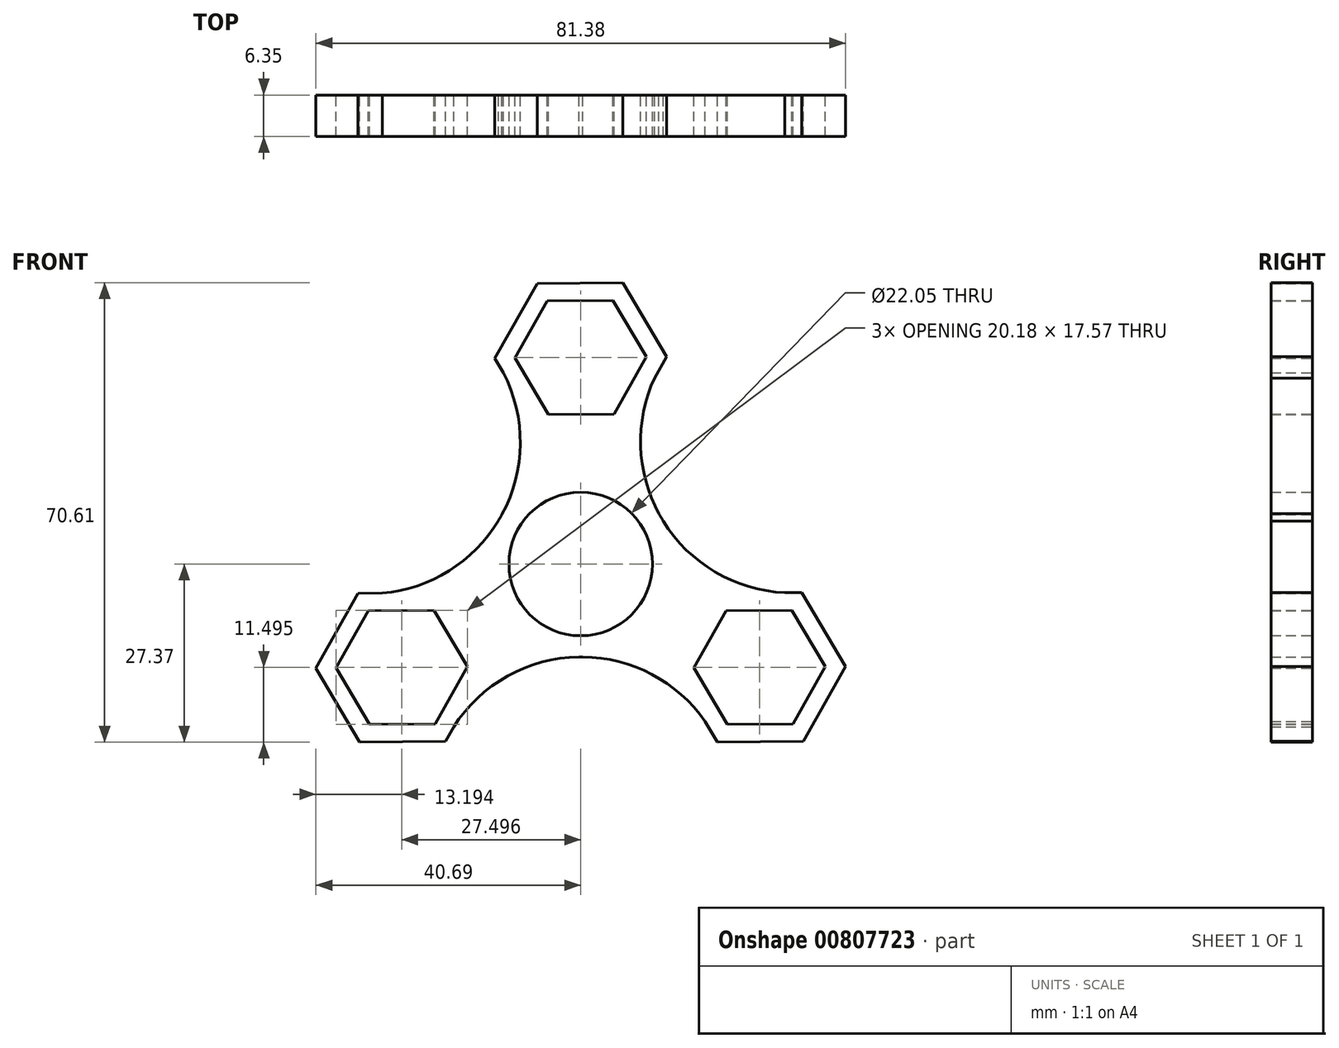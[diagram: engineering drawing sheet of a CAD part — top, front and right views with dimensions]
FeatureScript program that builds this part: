
annotation { "Feature Type Name" : "Feature", "Feature Type Description" : "" }
export const myFeature = defineFeature(function(context is Context, id is Id, definition is map)
    precondition{}
    {
        {
            var Q0;
            Q0=qCreatedBy(makeId("Front.planeOp"),FACE);
            var sketch = newSketch(context, id + "F0", { "sketchPlane" : qUnion([Q0])});
            skCircle(sketch, "E0", {"center": v(0, 0) * mm, "radius": 11.02 * mm});
            skCircle(sketch, "E1", {"center": v(0, 0) * mm, "radius": 14.29 * mm});
            skCircle(sketch, "E2.cCircle", {"center": v(0, 31.75) * mm, "radius": 11.43 * mm, "construction": true});
            skLineSegment(sketch, "E2.0", {"start": v(13.2, 31.87) * mm, "end": v(6.7, 20.38) * mm});
            skLineSegment(sketch, "E2.1", {"start": v(6.7, 20.38) * mm, "end": v(-6.5, 20.26) * mm});
            skLineSegment(sketch, "E2.2", {"start": v(-6.5, 20.26) * mm, "end": v(-13.2, 31.63) * mm});
            skLineSegment(sketch, "E2.3", {"start": v(-13.2, 31.63) * mm, "end": v(-6.7, 43.12) * mm});
            skLineSegment(sketch, "E2.4", {"start": v(-6.7, 43.12) * mm, "end": v(6.5, 43.24) * mm});
            skLineSegment(sketch, "E2.5", {"start": v(6.5, 43.24) * mm, "end": v(13.2, 31.87) * mm});
            skPoint(sketch, "E2.0.midPoint", {"position": v(9.95, 26.13) * mm});
            skCircle(sketch, "E3.cCircle", {"center": v(0, 31.75) * mm, "radius": 8.74 * mm, "construction": true});
            skLineSegment(sketch, "E3.0", {"start": v(-10.09, 31.66) * mm, "end": v(-5.13, 40.44) * mm});
            skLineSegment(sketch, "E3.1", {"start": v(-5.13, 40.44) * mm, "end": v(4.96, 40.53) * mm});
            skLineSegment(sketch, "E3.2", {"start": v(4.96, 40.53) * mm, "end": v(10.09, 31.84) * mm});
            skLineSegment(sketch, "E3.3", {"start": v(10.09, 31.84) * mm, "end": v(5.13, 23.06) * mm});
            skLineSegment(sketch, "E3.4", {"start": v(5.13, 23.06) * mm, "end": v(-4.96, 22.97) * mm});
            skLineSegment(sketch, "E3.5", {"start": v(-4.96, 22.97) * mm, "end": v(-10.09, 31.66) * mm});
            skPoint(sketch, "E3.0.midPoint", {"position": v(-7.6, 36.05) * mm});
            skCircle(sketch, "E4.1.0", {"center": v(-27.5, -15.87) * mm, "radius": 8.74 * mm, "construction": true});
            skLineSegment(sketch, "E4.1.1", {"start": v(-22.53, -7.1) * mm, "end": v(-17.4, -15.78) * mm});
            skLineSegment(sketch, "E4.1.2", {"start": v(-17.4, -15.78) * mm, "end": v(-22.37, -24.56) * mm});
            skLineSegment(sketch, "E4.1.3", {"start": v(-22.37, -24.56) * mm, "end": v(-32.46, -24.66) * mm});
            skLineSegment(sketch, "E4.1.4", {"start": v(-32.46, -24.66) * mm, "end": v(-37.59, -15.97) * mm});
            skLineSegment(sketch, "E4.1.5", {"start": v(-37.59, -15.97) * mm, "end": v(-32.62, -7.19) * mm});
            skLineSegment(sketch, "E4.1.6", {"start": v(-32.62, -7.19) * mm, "end": v(-22.53, -7.1) * mm});
            skLineSegment(sketch, "E4.1.7", {"start": v(-34.2, -4.5) * mm, "end": v(-21, -4.38) * mm});
            skCircle(sketch, "E4.1.8", {"center": v(-27.5, -15.87) * mm, "radius": 11.43 * mm, "construction": true});
            skLineSegment(sketch, "E4.1.9", {"start": v(-40.7, -16) * mm, "end": v(-34.2, -4.5) * mm});
            skLineSegment(sketch, "E4.1.10", {"start": v(-33.99, -27.37) * mm, "end": v(-40.7, -16) * mm});
            skLineSegment(sketch, "E4.1.11", {"start": v(-20.8, -27.24) * mm, "end": v(-33.99, -27.37) * mm});
            skLineSegment(sketch, "E4.1.12", {"start": v(-14.3, -15.75) * mm, "end": v(-20.8, -27.24) * mm});
            skLineSegment(sketch, "E4.1.13", {"start": v(-21, -4.38) * mm, "end": v(-14.3, -15.75) * mm});
            skCircle(sketch, "E4.2.0", {"center": v(27.5, -15.88) * mm, "radius": 8.74 * mm, "construction": true});
            skLineSegment(sketch, "E4.2.1", {"start": v(17.4, -15.97) * mm, "end": v(22.37, -7.19) * mm});
            skLineSegment(sketch, "E4.2.2", {"start": v(22.37, -7.19) * mm, "end": v(32.46, -7.1) * mm});
            skLineSegment(sketch, "E4.2.3", {"start": v(32.46, -7.1) * mm, "end": v(37.59, -15.78) * mm});
            skLineSegment(sketch, "E4.2.4", {"start": v(37.59, -15.78) * mm, "end": v(32.62, -24.56) * mm});
            skLineSegment(sketch, "E4.2.5", {"start": v(32.62, -24.56) * mm, "end": v(22.53, -24.66) * mm});
            skLineSegment(sketch, "E4.2.6", {"start": v(22.53, -24.66) * mm, "end": v(17.4, -15.97) * mm});
            skLineSegment(sketch, "E4.2.7", {"start": v(21, -27.37) * mm, "end": v(14.3, -16) * mm});
            skCircle(sketch, "E4.2.8", {"center": v(27.5, -15.88) * mm, "radius": 11.43 * mm, "construction": true});
            skLineSegment(sketch, "E4.2.9", {"start": v(34.2, -27.24) * mm, "end": v(21, -27.37) * mm});
            skLineSegment(sketch, "E4.2.10", {"start": v(40.7, -15.75) * mm, "end": v(34.2, -27.24) * mm});
            skLineSegment(sketch, "E4.2.11", {"start": v(33.99, -4.38) * mm, "end": v(40.7, -15.75) * mm});
            skLineSegment(sketch, "E4.2.12", {"start": v(20.8, -4.5) * mm, "end": v(33.99, -4.38) * mm});
            skLineSegment(sketch, "E4.2.13", {"start": v(14.3, -16) * mm, "end": v(20.8, -4.5) * mm});
            skArc(sketch, "E5", {"start": v(-34.2, -4.5) * mm, "mid": v(-12.43, 7) * mm, "end": v(-13.2, 31.63) * mm});
            skArc(sketch, "E6", {"start": v(21, -27.37) * mm, "mid": v(0.15, -14.28) * mm, "end": v(-20.8, -27.24) * mm});
            skArc(sketch, "E7", {"start": v(13.2, 31.87) * mm, "mid": v(12.28, 7.26) * mm, "end": v(33.99, -4.38) * mm});
            skSolve(sketch);
        }
        {
            var Q0;
            Q0 = qSketchRegion(id + "F0", true);
            extrude(context, id + "F1", {"entities" : qUnion([Q0]), "depth" : 6.35 * mm, "offsetDistance" : 25.4 * mm});
        }
    });
